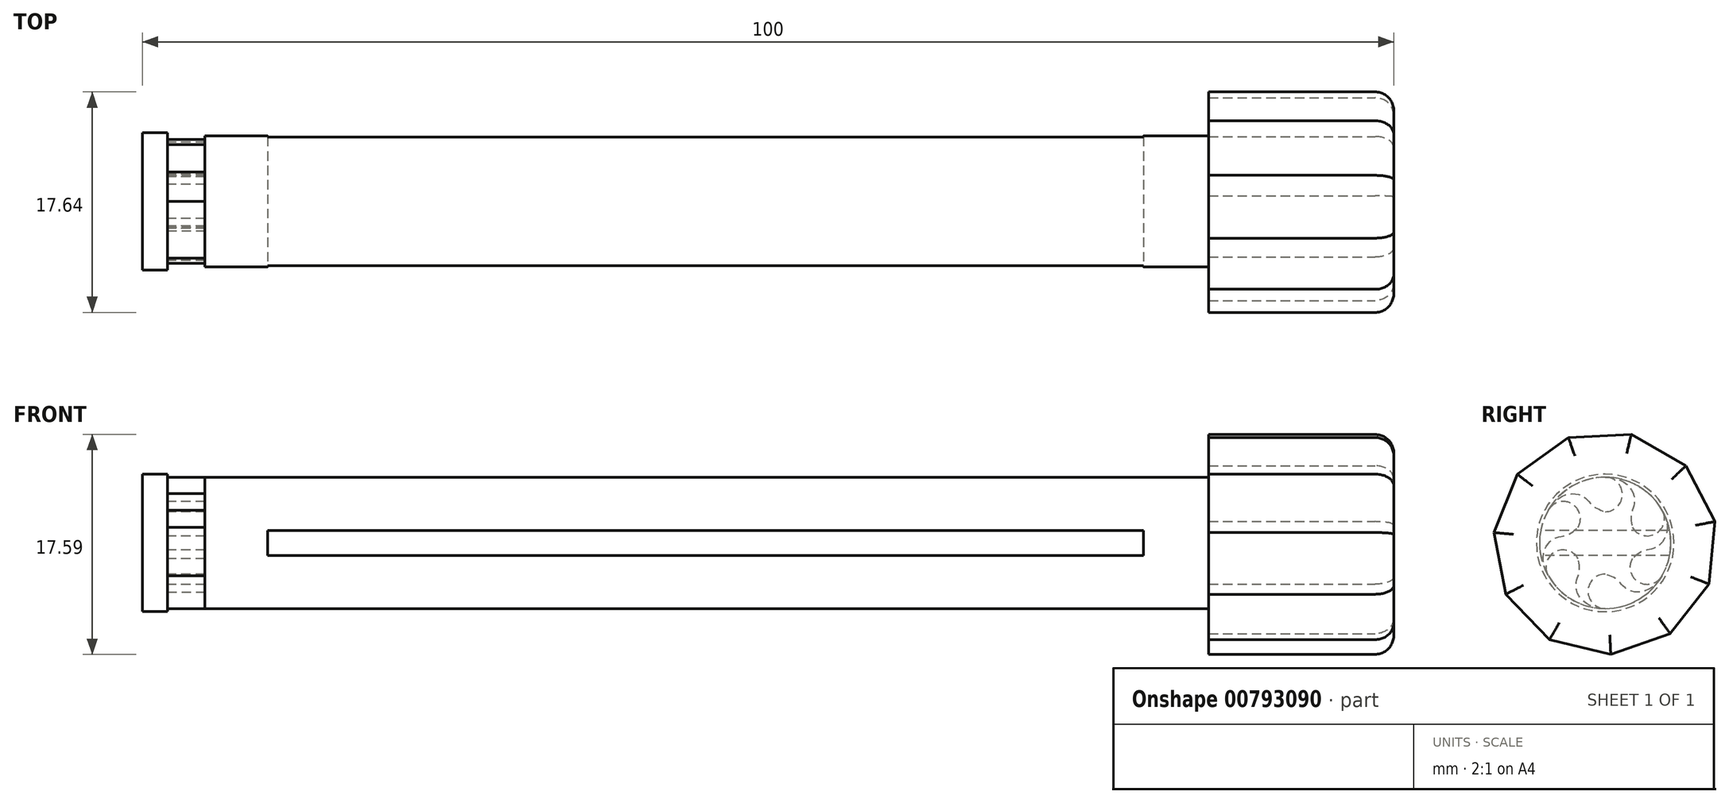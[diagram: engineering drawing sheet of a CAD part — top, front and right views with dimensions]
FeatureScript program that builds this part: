
annotation { "Feature Type Name" : "Feature", "Feature Type Description" : "" }
export const myFeature = defineFeature(function(context is Context, id is Id, definition is map)
    precondition{}
    {
        {
            var Q0;
            Q0=qCreatedBy(makeId("Right.planeOp"),FACE);
            var sketch = newSketch(context, id + "F0", { "sketchPlane" : qUnion([Q0])});
            skCircle(sketch, "E0", {"center": v(0, 0) * mm, "radius": 5.25 * mm});
            skSolve(sketch);
        }
        {
            var Q0;
            Q0=makeQuery(id+"F0.imprint","IMPRINT",FACE,{"disambiguationData":[TD([[makeQuery(id+"F0.imprint","IMPRINT",EDGE,{"derivedFrom":sQuery(id+"F0.wireOp",EDGE,"E0")}),1.0]])]});
            extrude(context, id + "F1", {"entities" : qUnion([Q0]), "endBound" : BoundingType.SYMMETRIC, "depth" : 90 * mm, "offsetDistance" : 25 * mm});
        }
        {
            var Q0;
            Q0=qCreatedBy(makeId("Front.planeOp"),FACE);
            var sketch = newSketch(context, id + "F2", { "sketchPlane" : qUnion([Q0])});
            skLineSegment(sketch, "E1.bottom", {"start": v(35, -1) * mm, "end": v(-35, -1) * mm});
            skLineSegment(sketch, "E1.top", {"start": v(35, 1) * mm, "end": v(-35, 1) * mm});
            skLineSegment(sketch, "E1.left", {"start": v(35, -1) * mm, "end": v(35, 1) * mm});
            skLineSegment(sketch, "E1.right", {"start": v(-35, -1) * mm, "end": v(-35, 1) * mm});
            skPoint(sketch, "E1.middle", {"position": v(0, 0) * mm});
            skSolve(sketch);
        }
        {
            var Q0;
            Q0 = qSketchRegion(id + "F2", true);
            extrude(context, id + "F3", {"entities" : qUnion([Q0]), "operationType" : NewBodyOperationType.REMOVE, "endBound" : BoundingType.SYMMETRIC, "oppositeDirection" : true, "depth" : 10 * mm, "offsetDistance" : 25 * mm});
        }
        {
            var Q0;
            Q0=makeQuery(id+"F1.opExtrude","CAP_FACE",FACE,{"disambiguationData":[OSD([sQuery(id+"F0.wireOp",EDGE,"E0")])],"isStart":true});
            var sketch = newSketch(context, id + "F4", { "sketchPlane" : qUnion([Q0])});
            skLineSegment(sketch, "E2", {"start": v(0, 0) * mm, "end": v(0, -5.25) * mm, "construction": true});
            skLineSegment(sketch, "E3", {"start": v(0, 0) * mm, "end": v(4.55, -2.63) * mm, "construction": true});
            skCircle(sketch, "E4", {"center": v(0, 0) * mm, "radius": 2.5 * mm});
            skLineSegment(sketch, "E5.MirrorCS", {"start": v(0, 0) * mm, "end": v(4.55, 2.62) * mm, "construction": true});
            skLineSegment(sketch, "E6.MirrorCS", {"start": v(0, 0) * mm, "end": v(0, 5.25) * mm, "construction": true});
            skLineSegment(sketch, "E7.MirrorCS", {"start": v(0, 0) * mm, "end": v(-4.55, 2.63) * mm, "construction": true});
            skLineSegment(sketch, "E8.MirrorCS", {"start": v(0, 0) * mm, "end": v(-4.55, -2.62) * mm, "construction": true});
            skArc(sketch, "E9", {"start": v(0, 5.25) * mm, "mid": v(-1.37, 3.88) * mm, "end": v(0, 2.5) * mm});
            skArc(sketch, "E10", {"start": v(-4.55, 2.63) * mm, "mid": v(-4.04, 0.75) * mm, "end": v(-2.17, 1.25) * mm});
            skArc(sketch, "E11", {"start": v(-4.55, -2.62) * mm, "mid": v(-2.67, -3.13) * mm, "end": v(-2.17, -1.25) * mm});
            skArc(sketch, "E12", {"start": v(0, -5.25) * mm, "mid": v(1.38, -3.88) * mm, "end": v(0, -2.5) * mm});
            skPoint(sketch, "E13", {"position": v(0, -2.62) * mm});
            skArc(sketch, "E14", {"start": v(4.55, -2.63) * mm, "mid": v(4.04, -0.75) * mm, "end": v(2.17, -1.25) * mm});
            skArc(sketch, "E15", {"start": v(4.55, 2.62) * mm, "mid": v(2.67, 3.13) * mm, "end": v(2.17, 1.25) * mm});
            skFitSpline(sketch, "E16", {"points": [v(0, 5.25) * mm, v(-2.34, 3.5) * mm, v(-2.09, 2.32) * mm, v(-2.17, 1.25) * mm], "startDerivative": vector(-10.96, 0.01) * mm, "endDerivative": vector(-0.74, -4.2) * mm});
            skFitSpline(sketch, "E17", {"points": [v(-4.55, 2.63) * mm, v(-4.2, -0.28) * mm, v(-3.05, -0.65) * mm, v(-2.17, -1.25) * mm], "startDerivative": vector(-5.49, -9.48) * mm, "endDerivative": vector(3.26, -2.74) * mm});
            skFitSpline(sketch, "E18", {"points": [v(-4.55, -2.62) * mm, v(-1.88, -3.78) * mm, v(-0.98, -2.97) * mm, v(0, -2.5) * mm], "startDerivative": vector(5.47, -9.5) * mm, "endDerivative": vector(4, 1.46) * mm});
            skFitSpline(sketch, "E19", {"points": [v(0, -5.25) * mm, v(2.33, -3.52) * mm, v(2.08, -2.34) * mm, v(2.17, -1.25) * mm], "startDerivative": vector(10.96, -0.01) * mm, "endDerivative": vector(0.74, 4.2) * mm});
            skFitSpline(sketch, "E20", {"points": [v(4.55, -2.63) * mm, v(4.21, 0.26) * mm, v(3.06, 0.63) * mm, v(2.17, 1.25) * mm], "startDerivative": vector(5.49, 9.48) * mm, "endDerivative": vector(-3.26, 2.74) * mm});
            skFitSpline(sketch, "E21", {"points": [v(4.55, 2.63) * mm, v(1.88, 3.78) * mm, v(0.98, 2.97) * mm, v(0, 2.5) * mm], "startDerivative": vector(-5.47, 9.5) * mm, "endDerivative": vector(-4, -1.46) * mm});
            skSolve(sketch);
        }
        {
            var Q0;
            Q0=makeQuery(id+"F4.imprint","IMPRINT",FACE,{"disambiguationData":[TD([[makeQuery(id+"F4.imprint","IMPRINT",EDGE,{"derivedFrom":sQuery(id+"F4.wireOp",EDGE,"06bcce8c-bce3-4937-bfc8-11742f9a7901")}),1.0]])]});
            var Q1;
            {var subQ0=sQuery(id+"F4.wireOp",EDGE,"E10");Q1=makeQuery(id+"F4.imprint","IMPRINT",FACE,{"disambiguationData":[TD([[makeQuery(id+"F4.imprint","IMPRINT",EDGE,{"derivedFrom":subQ0}),1.0]])]});}
            var Q2;
            {var subQ0=sQuery(id+"F4.wireOp",EDGE,"E9");Q2=makeQuery(id+"F4.imprint","IMPRINT",FACE,{"disambiguationData":[TD([[makeQuery(id+"F4.imprint","IMPRINT",EDGE,{"derivedFrom":subQ0}),1.0]])]});}
            var Q3;
            {var subQ0=sQuery(id+"F4.wireOp",EDGE,"E15");Q3=makeQuery(id+"F4.imprint","IMPRINT",FACE,{"disambiguationData":[TD([[makeQuery(id+"F4.imprint","IMPRINT",EDGE,{"derivedFrom":subQ0}),1.0]])]});}
            var Q4;
            {var subQ0=sQuery(id+"F4.wireOp",EDGE,"E14");Q4=makeQuery(id+"F4.imprint","IMPRINT",FACE,{"disambiguationData":[TD([[makeQuery(id+"F4.imprint","IMPRINT",EDGE,{"derivedFrom":subQ0}),1.0]])]});}
            var Q5;
            {var subQ0=sQuery(id+"F4.wireOp",EDGE,"E12");Q5=makeQuery(id+"F4.imprint","IMPRINT",FACE,{"disambiguationData":[TD([[makeQuery(id+"F4.imprint","IMPRINT",EDGE,{"derivedFrom":subQ0}),1.0]])]});}
            var Q6;
            {var subQ0=sQuery(id+"F4.wireOp",EDGE,"E11");Q6=makeQuery(id+"F4.imprint","IMPRINT",FACE,{"disambiguationData":[TD([[makeQuery(id+"F4.imprint","IMPRINT",EDGE,{"derivedFrom":subQ0}),1.0]])]});}
            extrude(context, id + "F5", {"entities" : qUnion([Q0, Q1, Q2, Q3, Q4, Q5, Q6]), "operationType" : NewBodyOperationType.REMOVE, "oppositeDirection" : true, "depth" : 5 * mm, "offsetDistance" : 25 * mm});
        }
        {
            var Q0;
            Q0 = qSketchRegion(id + "F2", true);
            extrude(context, id + "F6", {"entities" : qUnion([Q0]), "operationType" : NewBodyOperationType.REMOVE, "endBound" : BoundingType.SYMMETRIC, "oppositeDirection" : true, "depth" : 11 * mm, "offsetDistance" : 25 * mm});
        }
        {
            var Q0;
            Q0=makeQuery(id+"F1.opExtrude","CAP_FACE",FACE,{"disambiguationData":[OSD([sQuery(id+"F0.wireOp",EDGE,"E0")])],"isStart":false});
            var sketch = newSketch(context, id + "F7", { "sketchPlane" : qUnion([Q0])});
            skCircle(sketch, "E22.cCircle", {"center": v(0, 0) * mm, "radius": 8.56 * mm, "construction": true});
            skLineSegment(sketch, "E22.0", {"start": v(2.09, 8.68) * mm, "end": v(6.44, 6.17) * mm});
            skLineSegment(sketch, "E22.1", {"start": v(6.44, 6.17) * mm, "end": v(8.76, 1.7) * mm});
            skLineSegment(sketch, "E22.2", {"start": v(8.76, 1.7) * mm, "end": v(8.3, -3.3) * mm});
            skLineSegment(sketch, "E22.3", {"start": v(8.3, -3.3) * mm, "end": v(5.2, -7.26) * mm});
            skLineSegment(sketch, "E22.4", {"start": v(5.2, -7.26) * mm, "end": v(0.44, -8.91) * mm});
            skLineSegment(sketch, "E22.5", {"start": v(0.44, -8.91) * mm, "end": v(-4.44, -7.74) * mm});
            skLineSegment(sketch, "E22.6", {"start": v(-4.44, -7.74) * mm, "end": v(-7.92, -4.1) * mm});
            skLineSegment(sketch, "E22.7", {"start": v(-7.92, -4.1) * mm, "end": v(-8.88, 0.83) * mm});
            skLineSegment(sketch, "E22.8", {"start": v(-8.88, 0.83) * mm, "end": v(-7.03, 5.5) * mm});
            skLineSegment(sketch, "E22.9", {"start": v(-7.03, 5.5) * mm, "end": v(-2.94, 8.43) * mm});
            skLineSegment(sketch, "E22.10", {"start": v(-2.94, 8.43) * mm, "end": v(2.09, 8.68) * mm});
            skPoint(sketch, "E22.0.midPoint", {"position": v(4.26, 7.42) * mm});
            skSolve(sketch);
        }
        {
            var Q0;
            Q0 = qSketchRegion(id + "F7", true);
            extrude(context, id + "F8", {"entities" : qUnion([Q0]), "operationType" : NewBodyOperationType.ADD, "oppositeDirection" : true, "depth" : 4.8 * mm, "offsetDistance" : 25 * mm});
        }
        {
            var Q0;
            Q0=makeQuery(id+"F1.opExtrude","CAP_FACE",FACE,{"disambiguationData":[OSD([sQuery(id+"F0.wireOp",EDGE,"E0")])],"isStart":true});
            var sketch = newSketch(context, id + "F9", { "sketchPlane" : qUnion([Q0])});
            skCircle(sketch, "E23", {"center": v(0, 0) * mm, "radius": 5.5 * mm});
            skSolve(sketch);
        }
        {
            var Q0;
            Q0 = qSketchRegion(id + "F9", true);
            extrude(context, id + "F10", {"entities" : qUnion([Q0]), "operationType" : NewBodyOperationType.ADD, "oppositeDirection" : true, "depth" : 2 * mm, "offsetDistance" : 25 * mm});
        }
        {
            var Q0;
            Q0=makeQuery(id+"F8.boolean.opBoolean","MERGE",FACE,{"derivedFrom":[makeQuery(id+"F1.opExtrude","CAP_FACE",FACE,{"disambiguationData":[OSD([sQuery(id+"F0.wireOp",EDGE,"E0")])],"isStart":false}),makeQuery(id+"F8.opExtrude","CAP_FACE",FACE,{"disambiguationData":[OSD([sQuery(id+"F7.wireOp",EDGE,"E22.0"),sQuery(id+"F7.wireOp",EDGE,"E22.1"),sQuery(id+"F7.wireOp",EDGE,"E22.2"),sQuery(id+"F7.wireOp",EDGE,"E22.3"),sQuery(id+"F7.wireOp",EDGE,"E22.4"),sQuery(id+"F7.wireOp",EDGE,"E22.5"),sQuery(id+"F7.wireOp",EDGE,"E22.6"),sQuery(id+"F7.wireOp",EDGE,"E22.7"),sQuery(id+"F7.wireOp",EDGE,"E22.8"),sQuery(id+"F7.wireOp",EDGE,"E22.9"),sQuery(id+"F7.wireOp",EDGE,"E22.10")])],"isStart":true})]});
            extrude(context, id + "F11", {"entities" : qUnion([Q0]), "operationType" : NewBodyOperationType.ADD, "depth" : 10 * mm, "offsetDistance" : 25 * mm});
        }
        {
            var Q0;
            Q0=makeQuery(id+"F11.opExtrude","CAP_FACE",FACE,{"disambiguationData":[OSD([sQuery(id+"F0.wireOp",EDGE,"E0"),sQuery(id+"F7.wireOp",EDGE,"E22.0"),sQuery(id+"F7.wireOp",EDGE,"E22.1"),sQuery(id+"F7.wireOp",EDGE,"E22.2"),sQuery(id+"F7.wireOp",EDGE,"E22.3"),sQuery(id+"F7.wireOp",EDGE,"E22.4"),sQuery(id+"F7.wireOp",EDGE,"E22.5"),sQuery(id+"F7.wireOp",EDGE,"E22.6"),sQuery(id+"F7.wireOp",EDGE,"E22.7"),sQuery(id+"F7.wireOp",EDGE,"E22.8"),sQuery(id+"F7.wireOp",EDGE,"E22.9"),sQuery(id+"F7.wireOp",EDGE,"E22.10")])],"isStart":false});
            fillet(context, id + "F12", {"entities" : qUnion([Q0]), "tangentPropagation" : true, "radius" : 1.5 * mm, "defaultsChanged" : true, "vertexSettings" : [], "allowEdgeOverflow" : false});
        }
    });
